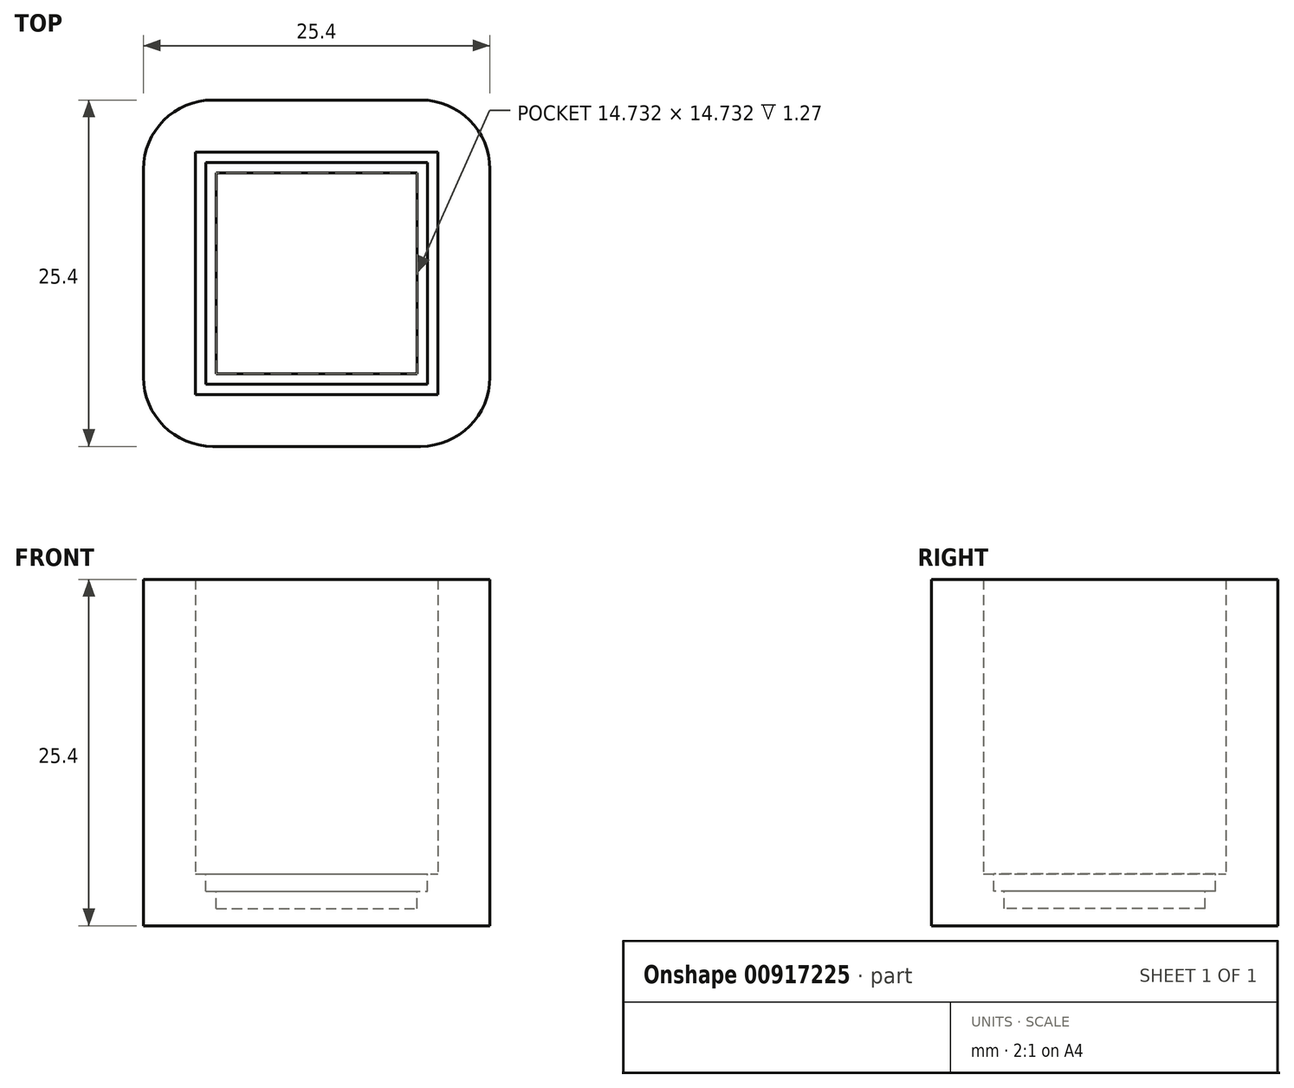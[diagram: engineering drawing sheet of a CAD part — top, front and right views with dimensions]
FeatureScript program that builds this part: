
annotation { "Feature Type Name" : "Feature", "Feature Type Description" : "" }
export const myFeature = defineFeature(function(context is Context, id is Id, definition is map)
    precondition{}
    {
        {
            var Q0;
            Q0=qCreatedBy(makeId("Front.planeOp"),FACE);
            var sketch = newSketch(context, id + "F0", { "sketchPlane" : qUnion([Q0])});
            skLineSegment(sketch, "E0.bottom", {"start": v(-46.65, 46) * mm, "end": v(-21.25, 46) * mm});
            skLineSegment(sketch, "E0.top", {"start": v(-46.65, 20.6) * mm, "end": v(-21.25, 20.6) * mm});
            skLineSegment(sketch, "E0.left", {"start": v(-46.65, 46) * mm, "end": v(-46.65, 20.6) * mm});
            skLineSegment(sketch, "E0.right", {"start": v(-21.25, 46) * mm, "end": v(-21.25, 20.6) * mm});
            skSolve(sketch);
        }
        {
            var Q0;
            Q0=makeQuery(id+"F0.imprint","IMPRINT",FACE,{"disambiguationData":[TD([[makeQuery(id+"F0.imprint","IMPRINT",EDGE,{"derivedFrom":sQuery(id+"F0.wireOp",EDGE,"E0.bottom")}),-1.0]])]});
            extrude(context, id + "F1", {"entities" : qUnion([Q0]), "depth" : 25.4 * mm, "offsetDistance" : 25.4 * mm});
        }
        {
            var Q0;
            Q0=makeQuery(id+"F1.opExtrude","SWEPT_FACE",FACE,{"disambiguationData":[OSD([sQuery(id+"F0.wireOp",EDGE,"E0.bottom")])]});
            shell(context, id + "F2", {"entities" : qUnion([Q0]), "thickness" : 3.8 * mm});
        }
        {
            var Q0;
            Q0=makeQuery(id+"F1.opExtrude","CAP_EDGE",EDGE,{"disambiguationData":[OSD([sQuery(id+"F0.wireOp",EDGE,"E0.left")])],"isStart":true});
            var Q1;
            Q1=makeQuery(id+"F1.opExtrude","CAP_EDGE",EDGE,{"disambiguationData":[OSD([sQuery(id+"F0.wireOp",EDGE,"E0.left")])],"isStart":false});
            var Q2;
            Q2=makeQuery(id+"F1.opExtrude","CAP_EDGE",EDGE,{"disambiguationData":[OSD([sQuery(id+"F0.wireOp",EDGE,"E0.right")])],"isStart":false});
            var Q3;
            Q3=makeQuery(id+"F1.opExtrude","CAP_EDGE",EDGE,{"disambiguationData":[OSD([sQuery(id+"F0.wireOp",EDGE,"E0.right")])],"isStart":true});
            fillet(context, id + "F3", {"entities" : qUnion([Q0, Q1, Q2, Q3]), "radius" : 5.08 * mm, "tangentPropagation" : true, "allowEdgeOverflow" : false});
        }
        {
            var Q0;
            Q0=makeQuery(id+"F2.opShell","OFFSET_FACE",FACE,{"disambiguationData":[OSD([sQuery(id+"F0.wireOp",EDGE,"E0.top")])]});
            var sketch = newSketch(context, id + "F4", { "sketchPlane" : qUnion([Q0])});
            skSolve(sketch);
        }
        {
            var Q0;
            {var subQ0=sQuery(id+"F0.wireOp",EDGE,"E0.top");Q0=makeQuery(id+"F4.imprint","IMPRINT",FACE,{"disambiguationData":[TD([[makeQuery(id+"F4.imprint","IMPRINT",EDGE,{"derivedFrom":makeQuery(id+"F2.opShell","OFFSET_EDGE",EDGE,{"disambiguationData":[OSD([subQ0]),TDD([makeQuery(id+"F1.opExtrude","CAP_EDGE",EDGE,{"disambiguationData":[OSD([subQ0])],"isStart":true})])]})}),-1.0]])]});}
            var sketch = newSketch(context, id + "F5", { "sketchPlane" : qUnion([Q0])});
            skLineSegment(sketch, "E1.bottom", {"start": v(-42.07, -4.57) * mm, "end": v(-25.82, -4.57) * mm});
            skLineSegment(sketch, "E1.top", {"start": v(-42.07, -20.83) * mm, "end": v(-25.82, -20.83) * mm});
            skLineSegment(sketch, "E1.left", {"start": v(-42.07, -4.57) * mm, "end": v(-42.07, -20.83) * mm});
            skLineSegment(sketch, "E1.right", {"start": v(-25.82, -4.57) * mm, "end": v(-25.82, -20.83) * mm});
            skSolve(sketch);
        }
        {
            var Q0;
            Q0 = qSketchRegion(id + "F5", true);
            extrude(context, id + "F6", {"entities" : qUnion([Q0]), "operationType" : NewBodyOperationType.REMOVE, "oppositeDirection" : true, "depth" : 1.27 * mm, "offsetDistance" : 25.4 * mm});
        }
        {
            var Q0;
            {var subQ0=sQuery(id+"F0.wireOp",EDGE,"E0.top");Q0=makeQuery(id+"F4.imprint","IMPRINT",FACE,{"disambiguationData":[TD([[makeQuery(id+"F4.imprint","IMPRINT",EDGE,{"derivedFrom":makeQuery(id+"F2.opShell","OFFSET_EDGE",EDGE,{"disambiguationData":[OSD([subQ0]),TDD([makeQuery(id+"F1.opExtrude","CAP_EDGE",EDGE,{"disambiguationData":[OSD([subQ0])],"isStart":true})])]})}),-1.0]])]});}
            var sketch = newSketch(context, id + "F7", { "sketchPlane" : qUnion([Q0])});
            skLineSegment(sketch, "E2.bottom", {"start": v(-41.31, -5.33) * mm, "end": v(-26.58, -5.33) * mm});
            skLineSegment(sketch, "E2.top", {"start": v(-41.31, -20.07) * mm, "end": v(-26.58, -20.07) * mm});
            skLineSegment(sketch, "E2.left", {"start": v(-41.31, -5.33) * mm, "end": v(-41.31, -20.07) * mm});
            skLineSegment(sketch, "E2.right", {"start": v(-26.58, -5.33) * mm, "end": v(-26.58, -20.07) * mm});
            skSolve(sketch);
        }
        {
            var Q0;
            Q0 = qSketchRegion(id + "F7", true);
            extrude(context, id + "F8", {"entities" : qUnion([Q0]), "operationType" : NewBodyOperationType.REMOVE, "oppositeDirection" : true, "depth" : 2.54 * mm, "offsetDistance" : 25.4 * mm});
        }
    });
